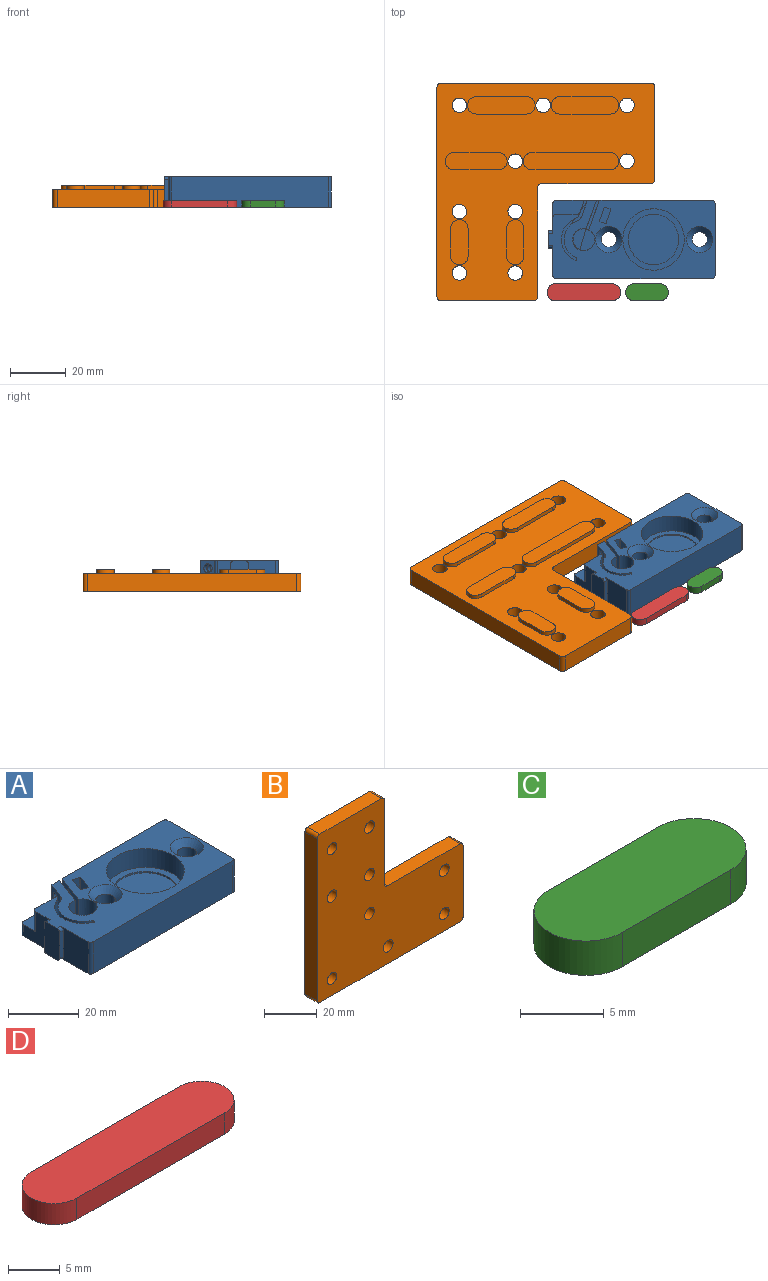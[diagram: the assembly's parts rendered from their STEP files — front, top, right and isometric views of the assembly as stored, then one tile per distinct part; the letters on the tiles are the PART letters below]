
ASSEMBLY  parts=4 mates=3
PART A: 89 faces, bbox 59.5x28x11 mm
  f0: plane 0.33x0.24mm, normal (0,0,-1), area 0mm2, adj f13,f29,f73
  f1: plane 59.5x28mm, normal (0,0,-1), area 1340.5mm2, adj f2,f24,f25,f26,f27,f44,f46,f53
  f2: plane 11x10.9mm, normal (-1,0,0), area 74.3mm2, adj f1,f12,f41,f51,f65,f66,f68,f69
  f3: cylinder r=0.3mm len=7.5mm, axis (0,0,1), area 3.6mm2, adj f4,f12,f21,f43
  f4: cylinder r=8mm len=14.77mm, axis (0,0,1), area 141.2mm2, adj f3,f5,f12,f43
  f5: cylinder r=3mm len=7.5mm, axis (0,0,1), area 13.8mm2, adj f4,f9,f12,f22,f43
  f6: cylinder r=0.3mm len=7.5mm, axis (0,0,1), area 2.7mm2, adj f7,f12,f27,f43
  f7: plane 10.43x7.5mm, normal (-0.94,0.34,0), area 73.8mm2, adj f6,f8,f12,f29,f39,f42,f43
  f8: cylinder r=3.8mm len=7.37mm, axis (0,0,1), area 6.2mm2, adj f7,f21,f42,f43
  f9: plane 5.07x1.85mm, normal (0.94,-0.34,0), area 2.7mm2, adj f5,f10,f22,f41,f43
  f10: cylinder r=0.3mm len=0.5mm, axis (0,0,1), area 0.3mm2, adj f9,f27,f41,f43
  f11: plane 20.85x11.42mm, normal (0,0,-1), area 68.7mm2, adj f13,f14,f15,f16,f17,f18,f19,f20
  f12: plane 59.5x28mm, normal (0,0,1), area 957.2mm2, adj f2,f3,f4,f5,f6,f7,f13,f14
  f13: plane 9.7x7mm, normal (0.94,-0.34,0), area 64.2mm2, adj f0,f11,f12,f14,f29,f40
  f14: cylinder r=0.3mm len=7.5mm, axis (0,0,1), area 5mm2, adj f11,f12,f13,f15,f43
  f15: plane 7x2.55mm, normal (0,1,0), area 17.9mm2, adj f11,f12,f14,f16
  f16: cylinder r=0.3mm len=7mm, axis (0,0,1), area 2.6mm2, adj f11,f12,f15,f17
  f17: plane 7x5.46mm, normal (-0.94,0.34,0), area 32.7mm2, adj f11,f12,f16,f18,f40
  f18: cylinder r=3mm len=7mm, axis (0,0,1), area 18.1mm2, adj f11,f12,f17,f19
  f19: cylinder r=7mm len=13.03mm, axis (0,0,1), area 117.3mm2, adj f11,f12,f18,f20,f75
  f20: cylinder r=0.3mm len=7mm, axis (0,0,1), area 3.2mm2, adj f11,f12,f19,f21
  f21: plane 7.5x3.66mm, normal (-0.94,0.34,0), area 4.7mm2, adj f3,f8,f11,f12,f20,f42,f43
  f22: cylinder r=0.3mm len=7mm, axis (0,0,1), area 4.5mm2, adj f5,f9,f12,f23,f41
  f23: plane 8x7mm, normal (0,1,0), area 56mm2, adj f12,f22,f41,f69
  f24: plane 11x10.9mm, normal (-1,0,0), area 109.3mm2, adj f1,f12,f52,f64,f67,f70
  f25: plane 56x11mm, normal (0,-1,0), area 616mm2, adj f1,f12,f70,f71
  f26: plane 26x11mm, normal (1,0,0), area 286mm2, adj f1,f12,f71,f72
  f27: plane 56x11mm, normal (0,1,0), area 502.1mm2, adj f1,f6,f10,f12,f41,f43,f68,f72
  f28: cylinder r=11mm len=22mm, axis (0,0,1), area 449.2mm2, adj f12,f49
  f29: cylinder r=4mm len=8mm, axis (0,0,1), area 168.9mm2, adj f0,f7,f11,f12,f13,f42
  f30: plane 5.5x4.6mm, normal (-0.94,0.34,0), area 27mm2, adj f12,f31,f37,f38
  f31: cylinder r=0.3mm len=5.5mm, axis (0,0,1), area 2.6mm2, adj f12,f30,f32,f38
  f32: plane 5.5x1.79mm, normal (-0.34,-0.94,0), area 10.4mm2, adj f12,f31,f33,f38
  f33: cylinder r=0.3mm len=5.5mm, axis (0,0,1), area 2.6mm2, adj f12,f32,f34,f38
  f34: plane 5.5x4.6mm, normal (0.94,-0.34,0), area 18.9mm2, adj f12,f33,f35,f38,f39
  f35: cylinder r=0.3mm len=5.5mm, axis (0,0,1), area 2.6mm2, adj f12,f34,f36,f38
  f36: plane 5.5x1.79mm, normal (0.34,0.94,0), area 10.4mm2, adj f12,f35,f37,f38
  f37: cylinder r=0.3mm len=5.5mm, axis (0,0,1), area 2.6mm2, adj f12,f30,f36,f38
  f38: plane 5.85x4.06mm, normal (0,0,1), area 13.7mm2, adj f30,f31,f32,f33,f34,f35,f36,f37
  f39: cylinder r=1.6mm len=3.86mm, axis (0.94,-0.34,0), area 25.1mm2, adj f7,f34
  f40: cylinder r=1.6mm len=4.03mm, axis (0.94,-0.34,0), area 30.2mm2, adj f13,f17
  f41: plane 11.11x6mm, normal (0,0,1), area 51.6mm2, adj f2,f9,f10,f22,f23,f27,f68,f69
  f42: plane 7.8x7.8mm, normal (0,0,1), area 47.7mm2, adj f7,f8,f21,f29
  f43: plane 21.43x13.84mm, normal (0,0,1), area 108.9mm2, adj f3,f4,f5,f6,f7,f8,f9,f10
  f44: cylinder r=2.75mm len=9.05mm, axis (0,0,1), area 156.4mm2, adj f1,f45
  f45: cone r=2.75mm half-angle=45deg, axis (0,0,1), area 64.5mm2, adj f12,f44
  f46: cylinder r=2.75mm len=9.05mm, axis (0,0,1), area 156.4mm2, adj f1,f47
  f47: cone r=2.75mm half-angle=45deg, axis (0,0,1), area 64.5mm2, adj f12,f46
  f48: cylinder r=9mm len=18mm, axis (0,0,-1), area 28.3mm2, adj f49,f50
  f49: plane 22x22mm, normal (0,0,1), area 125.7mm2, adj f28,f48
  f50: plane 18x18mm, normal (0,0,1), area 254.5mm2, adj f48
  f51: plane 9x1.5mm, normal (0,1,0), area 13.5mm2, adj f2,f53,f65,f66
  f52: plane 9x1.5mm, normal (0,-1,0), area 13.5mm2, adj f24,f53,f64,f67
  f53: plane 11x6.2mm, normal (-1,0,0), area 67.3mm2, adj f1,f12,f51,f52,f64,f65,f66,f67
  f54: cylinder r=3.1mm len=6.2mm, axis (0,0,-1), area 14.6mm2, adj f1,f55,f57,f58
  f55: plane 9.1x1.5mm, normal (0,-1,0), area 13.7mm2, adj f1,f54,f56,f58
  f56: cylinder r=3.1mm len=6.2mm, axis (0,0,-1), area 14.6mm2, adj f1,f55,f57,f58
  f57: plane 9.1x1.5mm, normal (0,1,0), area 13.7mm2, adj f1,f54,f56,f58
  f58: plane 15.3x6.2mm, normal (0,0,-1), area 86.6mm2, adj f54,f55,f56,f57
  f59: cylinder r=3.1mm len=6.2mm, axis (0,0,-1), area 14.6mm2, adj f1,f60,f62,f63
  f60: plane 20.1x1.5mm, normal (0,-1,0), area 30.1mm2, adj f1,f59,f61,f63
  f61: cylinder r=3.1mm len=6.2mm, axis (0,0,-1), area 14.6mm2, adj f1,f60,f62,f63
  f62: plane 20.1x1.5mm, normal (0,1,0), area 30.1mm2, adj f1,f59,f61,f63
  f63: plane 26.3x6.2mm, normal (0,0,-1), area 154.8mm2, adj f59,f60,f61,f62
  f64: cylinder r=1mm len=1.5mm, axis (1,0,0), area 2.4mm2, adj f12,f24,f52,f53
  f65: cylinder r=1mm len=1.5mm, axis (-1,0,0), area 2.4mm2, adj f2,f12,f51,f53
  f66: cylinder r=1mm len=1.5mm, axis (-1,0,0), area 2.4mm2, adj f1,f2,f51,f53
  f67: cylinder r=1mm len=1.5mm, axis (1,0,0), area 2.4mm2, adj f1,f24,f52,f53
  f68: cylinder r=1mm len=4mm, axis (0,0,1), area 6.3mm2, adj f1,f2,f27,f41
  f69: cylinder r=1mm len=7mm, axis (0,0,-1), area 11mm2, adj f2,f12,f23,f41
  f70: cylinder r=1mm len=11mm, axis (0,0,-1), area 17.3mm2, adj f1,f12,f24,f25
  f71: cylinder r=1mm len=11mm, axis (0,0,1), area 17.3mm2, adj f1,f12,f25,f26
  f72: cylinder r=1mm len=11mm, axis (0,0,-1), area 17.3mm2, adj f1,f12,f26,f27
  f73: cylinder r=0.3mm len=0.6mm, axis (0,0,1), area 0.9mm2, adj f0,f11,f43
  f74: cylinder r=0.3mm len=0.6mm, axis (0,0,1), area 0.9mm2, adj f11,f43,f75
  f75: plane 0.12x0.05mm, normal (0,0,1), area 0mm2, adj f19,f74
  f76: cylinder r=0.3mm len=0.6mm, axis (0,0,1), area 0.9mm2, adj f11,f43
  f77: cylinder r=0.3mm len=0.6mm, axis (0,0,1), area 0.9mm2, adj f11,f43
  f78: cylinder r=0.3mm len=0.6mm, axis (0,0,1), area 0.9mm2, adj f11,f43
  f79: cylinder r=0.3mm len=0.6mm, axis (0,0,1), area 0.9mm2, adj f11,f43
  f80: cylinder r=0.3mm len=0.6mm, axis (0,0,1), area 0.9mm2, adj f11,f43
  f81: cylinder r=0.3mm len=0.6mm, axis (0,0,1), area 0.9mm2, adj f11,f43
  f82: cylinder r=0.3mm len=0.6mm, axis (0,0,1), area 0.9mm2, adj f11,f43
  f83: cylinder r=0.3mm len=0.6mm, axis (0,0,1), area 0.9mm2, adj f11,f43
  f84: cylinder r=0.3mm len=0.6mm, axis (0,0,1), area 0.9mm2, adj f11,f43
  f85: cylinder r=0.3mm len=0.6mm, axis (0,0,1), area 0.9mm2, adj f11,f43
  f86: cylinder r=0.3mm len=0.6mm, axis (0,0,1), area 0.9mm2, adj f11,f43
  f87: cylinder r=0.3mm len=0.6mm, axis (0,0,1), area 0.9mm2, adj f11,f43
  f88: cylinder r=0.3mm len=0.6mm, axis (0,0,1), area 0.9mm2, adj f11,f43
PART B: 53 faces, bbox 78x8x78 mm
  f0: plane 39x6.5mm, normal (0,0,1), area 253.5mm2, adj f6,f7,f47,f52
  f1: plane 39x6.5mm, normal (1,0,0), area 253.5mm2, adj f6,f7,f47,f48
  f2: plane 33x6.5mm, normal (0,0,1), area 214.5mm2, adj f6,f7,f48,f49
  f3: plane 75x6.5mm, normal (-1,0,0), area 487.5mm2, adj f6,f7,f49,f50
  f4: plane 75x6.5mm, normal (0,0,-1), area 487.5mm2, adj f6,f7,f50,f51
  f5: plane 33x6.5mm, normal (1,0,0), area 214.5mm2, adj f6,f7,f51,f52
  f6: plane 78x78mm, normal (0,1,0), area 3325.8mm2, adj f0,f1,f2,f3,f4,f5,f8,f9
  f7: plane 78x78mm, normal (0,-1,0), area 4126.9mm2, adj f0,f1,f2,f3,f4,f5,f8,f9
  f8: cylinder r=2.6mm len=6.5mm, axis (0,-1,0), area 106.2mm2, adj f6,f7
  f9: cylinder r=2.6mm len=6.5mm, axis (0,-1,0), area 106.2mm2, adj f6,f7
  f10: cylinder r=2.6mm len=6.5mm, axis (0,-1,0), area 106.2mm2, adj f6,f7
  f11: cylinder r=2.6mm len=6.5mm, axis (0,-1,0), area 106.2mm2, adj f6,f7
  f12: cylinder r=2.6mm len=6.5mm, axis (0,-1,0), area 106.2mm2, adj f6,f7
  f13: cylinder r=2.6mm len=6.5mm, axis (0,-1,0), area 106.2mm2, adj f6,f7
  f14: cylinder r=2.6mm len=6.5mm, axis (0,-1,0), area 106.2mm2, adj f6,f7
  f15: cylinder r=2.6mm len=6.5mm, axis (0,-1,0), area 106.2mm2, adj f6,f7
  f16: cylinder r=2.6mm len=6.5mm, axis (0,-1,0), area 106.2mm2, adj f6,f7
  f17: cylinder r=3.1mm len=6.2mm, axis (0,-1,0), area 14.6mm2, adj f6,f18,f20,f21
  f18: plane 28x1.5mm, normal (0,0,1), area 42mm2, adj f6,f17,f19,f21
  f19: cylinder r=3.1mm len=6.2mm, axis (0,-1,0), area 14.6mm2, adj f6,f18,f20,f21
  f20: plane 28x1.5mm, normal (0,0,-1), area 42mm2, adj f6,f17,f19,f21
  f21: plane 34.2x6.2mm, normal (0,1,0), area 203.8mm2, adj f17,f18,f19,f20
  f22: cylinder r=3.1mm len=6.2mm, axis (0,-1,0), area 14.6mm2, adj f6,f23,f25,f26
  f23: plane 18x1.5mm, normal (0,0,1), area 27mm2, adj f6,f22,f24,f26
  f24: cylinder r=3.1mm len=6.2mm, axis (0,-1,0), area 14.6mm2, adj f6,f23,f25,f26
  f25: plane 18x1.5mm, normal (0,0,-1), area 27mm2, adj f6,f22,f24,f26
  f26: plane 24.2x6.2mm, normal (0,1,0), area 141.8mm2, adj f22,f23,f24,f25
  f27: cylinder r=3.1mm len=6.2mm, axis (0,-1,0), area 14.6mm2, adj f6,f28,f30,f31
  f28: plane 18x1.5mm, normal (0,0,1), area 27mm2, adj f6,f27,f29,f31
  f29: cylinder r=3.1mm len=6.2mm, axis (0,-1,0), area 14.6mm2, adj f6,f28,f30,f31
  f30: plane 18x1.5mm, normal (0,0,-1), area 27mm2, adj f6,f27,f29,f31
  f31: plane 24.2x6.2mm, normal (0,1,0), area 141.8mm2, adj f27,f28,f29,f30
  f32: cylinder r=3.1mm len=6.2mm, axis (0,-1,0), area 14.6mm2, adj f6,f33,f35,f36
  f33: plane 10x1.5mm, normal (1,0,0), area 15mm2, adj f6,f32,f34,f36
  f34: cylinder r=3.1mm len=6.2mm, axis (0,-1,0), area 14.6mm2, adj f6,f33,f35,f36
  f35: plane 10x1.5mm, normal (-1,0,0), area 15mm2, adj f6,f32,f34,f36
  f36: plane 16.2x6.2mm, normal (0,1,0), area 92.2mm2, adj f32,f33,f34,f35
  f37: cylinder r=3.1mm len=6.2mm, axis (0,-1,0), area 14.6mm2, adj f6,f38,f40,f41
  f38: plane 10x1.5mm, normal (1,0,0), area 15mm2, adj f6,f37,f39,f41
  f39: cylinder r=3.1mm len=6.2mm, axis (0,-1,0), area 14.6mm2, adj f6,f38,f40,f41
  f40: plane 10x1.5mm, normal (-1,0,0), area 15mm2, adj f6,f37,f39,f41
  f41: plane 16.2x6.2mm, normal (0,1,0), area 92.2mm2, adj f37,f38,f39,f40
  f42: cylinder r=3.1mm len=6.2mm, axis (0,-1,0), area 14.6mm2, adj f6,f43,f45,f46
  f43: plane 16x1.5mm, normal (0,0,1), area 24mm2, adj f6,f42,f44,f46
  f44: cylinder r=3.1mm len=6.2mm, axis (0,-1,0), area 14.6mm2, adj f6,f43,f45,f46
  f45: plane 16x1.5mm, normal (0,0,-1), area 24mm2, adj f6,f42,f44,f46
  f46: plane 22.2x6.2mm, normal (0,1,0), area 129.4mm2, adj f42,f43,f44,f45
  f47: cylinder r=1.5mm len=6.5mm, axis (0,1,0), area 15.3mm2, adj f0,f1,f6,f7
  f48: cylinder r=1.5mm len=6.5mm, axis (0,-1,0), area 15.3mm2, adj f1,f2,f6,f7
  f49: cylinder r=1.5mm len=6.5mm, axis (0,-1,0), area 15.3mm2, adj f2,f3,f6,f7
  f50: cylinder r=1.5mm len=6.5mm, axis (0,-1,0), area 15.3mm2, adj f3,f4,f6,f7
  f51: cylinder r=1.5mm len=6.5mm, axis (0,-1,0), area 15.3mm2, adj f4,f5,f6,f7
  f52: cylinder r=1.5mm len=6.5mm, axis (0,-1,0), area 15.3mm2, adj f0,f5,f6,f7
PART C: 6 faces, bbox 15.3x6.2x2.5 mm
  f0: cylinder r=3.1mm len=6.2mm, axis (0,0,1), area 24.3mm2, adj f1,f3,f4,f5
  f1: plane 9.1x2.5mm, normal (0,1,0), area 22.8mm2, adj f0,f2,f4,f5
  f2: cylinder r=3.1mm len=6.2mm, axis (0,0,1), area 24.3mm2, adj f1,f3,f4,f5
  f3: plane 9.1x2.5mm, normal (0,-1,0), area 22.8mm2, adj f0,f2,f4,f5
  f4: plane 15.3x6.2mm, normal (0,0,-1), area 86.6mm2, adj f0,f1,f2,f3
  f5: plane 15.3x6.2mm, normal (0,0,1), area 86.6mm2, adj f0,f1,f2,f3
PART D: 6 faces, bbox 26.3x6.2x2.5 mm
  f0: cylinder r=3.1mm len=6.2mm, axis (0,0,1), area 24.3mm2, adj f1,f3,f4,f5
  f1: plane 20.1x2.5mm, normal (0,1,0), area 50.3mm2, adj f0,f2,f4,f5
  f2: cylinder r=3.1mm len=6.2mm, axis (0,0,1), area 24.3mm2, adj f1,f3,f4,f5
  f3: plane 20.1x2.5mm, normal (0,-1,0), area 50.3mm2, adj f0,f2,f4,f5
  f4: plane 26.3x6.2mm, normal (0,0,-1), area 154.8mm2, adj f0,f1,f2,f3
  f5: plane 26.3x6.2mm, normal (0,0,1), area 154.8mm2, adj f0,f1,f2,f3
PLACE A t=(19.06,-58,11)mm
PLACE B rot(axis=(1,0,0),90deg) t=(8,-8,0)mm
PLACE C t=(43.46,-76.9,17.5)mm
PLACE D t=(-6.14,-76.9,17.5)mm
MATE fastened B.f7 <-> A.f1  axis (0,0,-1) through (6.5,-50,0)mm
MATE fastened B.f7 <-> D.f4  axis (0,0,-1) through (6.5,-50,0)mm
MATE fastened D.f4 <-> C.f4  axis (0,0,-1) through (34.6,-50,0)mm
